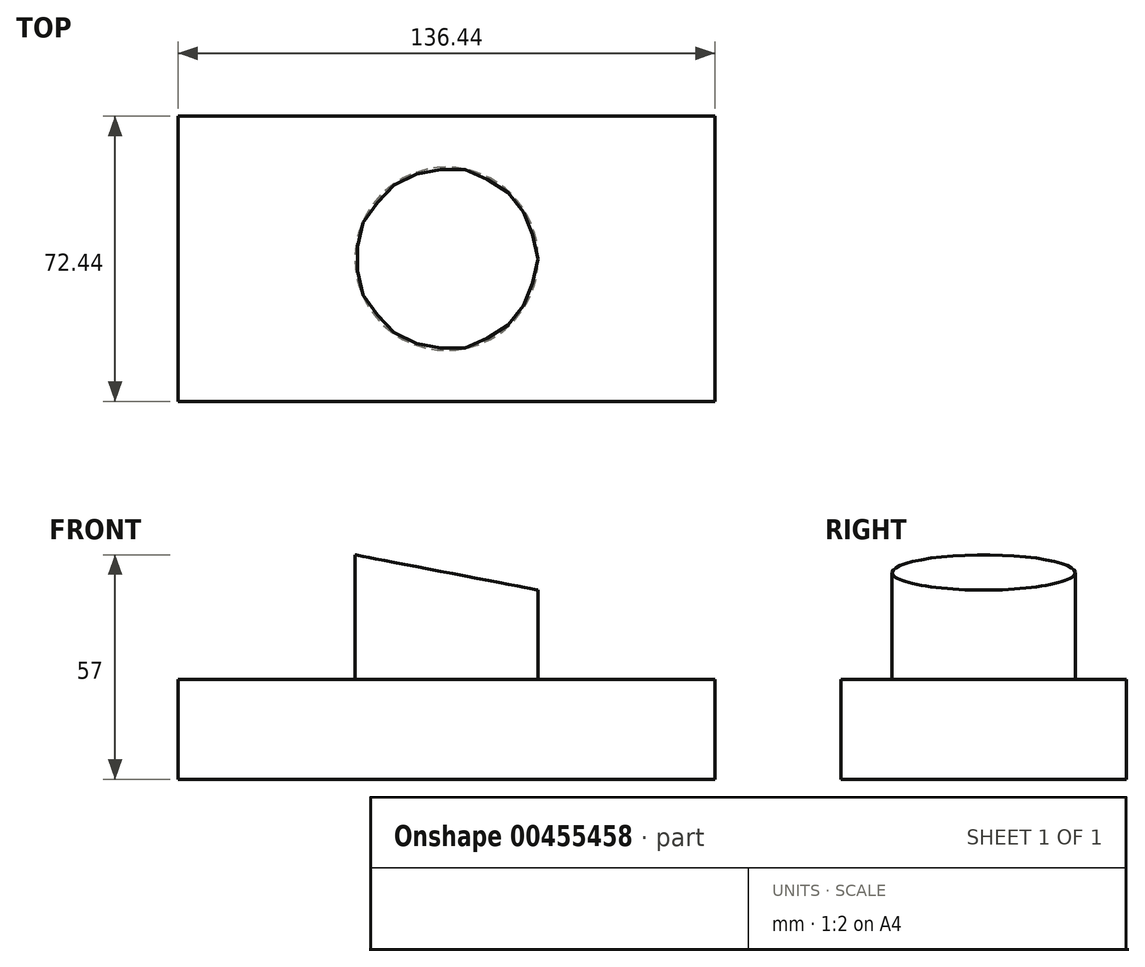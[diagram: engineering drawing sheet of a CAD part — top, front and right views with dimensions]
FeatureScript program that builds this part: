
annotation { "Feature Type Name" : "Feature", "Feature Type Description" : "" }
export const myFeature = defineFeature(function(context is Context, id is Id, definition is map)
    precondition{}
    {
        {
            var Q0;
            Q0=qCreatedBy(makeId("Top.planeOp"),FACE);
            var sketch = newSketch(context, id + "F0", { "sketchPlane" : qUnion([Q0])});
            skLineSegment(sketch, "E0.bottom", {"start": v(68.22, 36.22) * mm, "end": v(-68.22, 36.22) * mm});
            skLineSegment(sketch, "E0.top", {"start": v(68.22, -36.22) * mm, "end": v(-68.22, -36.22) * mm});
            skLineSegment(sketch, "E0.left", {"start": v(68.22, 36.22) * mm, "end": v(68.22, -36.22) * mm});
            skLineSegment(sketch, "E0.right", {"start": v(-68.22, 36.22) * mm, "end": v(-68.22, -36.22) * mm});
            skPoint(sketch, "E0.middle", {"position": v(0, 0) * mm});
            skSolve(sketch);
        }
        {
            var Q0;
            Q0=makeQuery(id+"F0.imprint","IMPRINT",FACE,{"disambiguationData":[TD([[makeQuery(id+"F0.imprint","IMPRINT",EDGE,{"derivedFrom":sQuery(id+"F0.wireOp",EDGE,"E0.bottom")}),1.0]])]});
            extrude(context, id + "F1", {"entities" : qUnion([Q0]), "depth" : 25.4 * mm});
        }
        {
            var Q0;
            Q0=makeQuery(id+"F1.opExtrude","CAP_FACE",FACE,{"disambiguationData":[OSD([sQuery(id+"F0.wireOp",EDGE,"E0.bottom"),sQuery(id+"F0.wireOp",EDGE,"E0.top"),sQuery(id+"F0.wireOp",EDGE,"E0.left"),sQuery(id+"F0.wireOp",EDGE,"E0.right")])],"isStart":false});
            var sketch = newSketch(context, id + "F2", { "sketchPlane" : qUnion([Q0])});
            skCircle(sketch, "E1", {"center": v(0, 0) * mm, "radius": 23.27 * mm});
            skSolve(sketch);
        }
        {
            var Q0;
            Q0=makeQuery(id+"F2.imprint","IMPRINT",FACE,{"disambiguationData":[TD([[makeQuery(id+"F2.imprint","IMPRINT",EDGE,{"derivedFrom":sQuery(id+"F2.wireOp",EDGE,"E1")}),1.0]])]});
            extrude(context, id + "F3", {"entities" : qUnion([Q0]), "operationType" : NewBodyOperationType.ADD, "depth" : 36.32 * mm});
        }
        {
            var Q0;
            Q0=qCreatedBy(makeId("Front.planeOp"),FACE);
            var sketch = newSketch(context, id + "F4", { "sketchPlane" : qUnion([Q0])});
            skLineSegment(sketch, "E2", {"start": v(-68.5, 65.7) * mm, "end": v(54.18, 42.11) * mm});
            skLineSegment(sketch, "E3", {"start": v(54.18, 42.11) * mm, "end": v(54.18, 69.62) * mm});
            skLineSegment(sketch, "E4", {"start": v(54.18, 69.62) * mm, "end": v(-68.5, 65.7) * mm});
            skSolve(sketch);
        }
        {
            var Q0;
            Q0=makeQuery(id+"F4.imprint","IMPRINT",FACE,{"disambiguationData":[TD([[makeQuery(id+"F4.imprint","IMPRINT",EDGE,{"derivedFrom":sQuery(id+"F4.wireOp",EDGE,"E2")}),1.0]])]});
            extrude(context, id + "F5", {"entities" : qUnion([Q0]), "operationType" : NewBodyOperationType.REMOVE, "oppositeDirection" : true, "depth" : 25.4 * mm, "hasSecondDirection" : true, "secondDirectionOppositeDirection" : false, "secondDirectionDepth" : 25.4 * mm});
        }
    });
